# Revit family: Skystar_SK_42-E-2tr-HTA800_RFA2018
name_source: partatom
category: Mechanical Equipment
revit_build: Autodesk Revit LT 2018 (Build: 20180329_1100(x64)
units: mm (PartAtom-declared; Revit-internal decimal feet)

## family parameters
Always vertical = Yes
Cut with Voids When Loaded = Yes
OmniClass Number = 23.75.00.00
OmniClass Title = Climate Control (HVAC)
Part Type = Normal
Room Calculation Point = Yes
Round Connector Dimension = Use Diameter
Shared = Yes
Work Plane-Based = Yes

## types (3) — shared parameters
4Pipes = No
A = 819 mm  [stored 2.68701 ft]
D_QC_IN = 20 mm  [stored 0.0656168 ft]
D_Q_C_OUT = 20 mm  [stored 0.0656168 ft]
Default Elevation = 1219 mm
Description = Kazetový fancoil
Electric Battery = Yes
Foro controsoffitto = 829 mm
Lookup Table Name = SABIANA-SkyStar
Manufacturer = Hydronix
S = 348 mm
THIN_def = 50 °C
Type Comments = Výměník dvoutrubkový; elektrický ohřev; motor asynchronní 3-otáčkový; čelní deska, mřížka, výdechy z ABS bílá RAL 9003
Type Image = 800x800.jpg
URL = www.hydronix.cz
cpa = 1.0050 J/(g·°C)
cph = 4.1860 J/(g·°C)
rho_a = 1.2000 kg/m³
rho_h = 1000.2970 kg/m³
side machine = 819 mm  [stored 2.68701 ft]
zero-valued in all types: BVc

## per-type parameters (varying)
| type | Assembly Code | Model | Taglia |
| SK42-E | SK42- (o.č.: 0079063)+HTA800 (o.č.: 9079035) | SK 42-E | 42 |
| SK62-E | SK62-E (o.č.: 0079065)+HTA800 (o.č.: 9079035) | SK 62-E | 62 |
| SK52-E | SK52-E (o.č.: 0079064)+HTA800 (o.č.: 9079035) | SK 52-E | 52 |

note: [stored X ft] marks values corroborated as IEEE doubles in the binary element streams (Revit-internal decimal feet)

## geometry (parser evidence)
native form markers: Blend x2
no freeform markers — native parametric forms only
